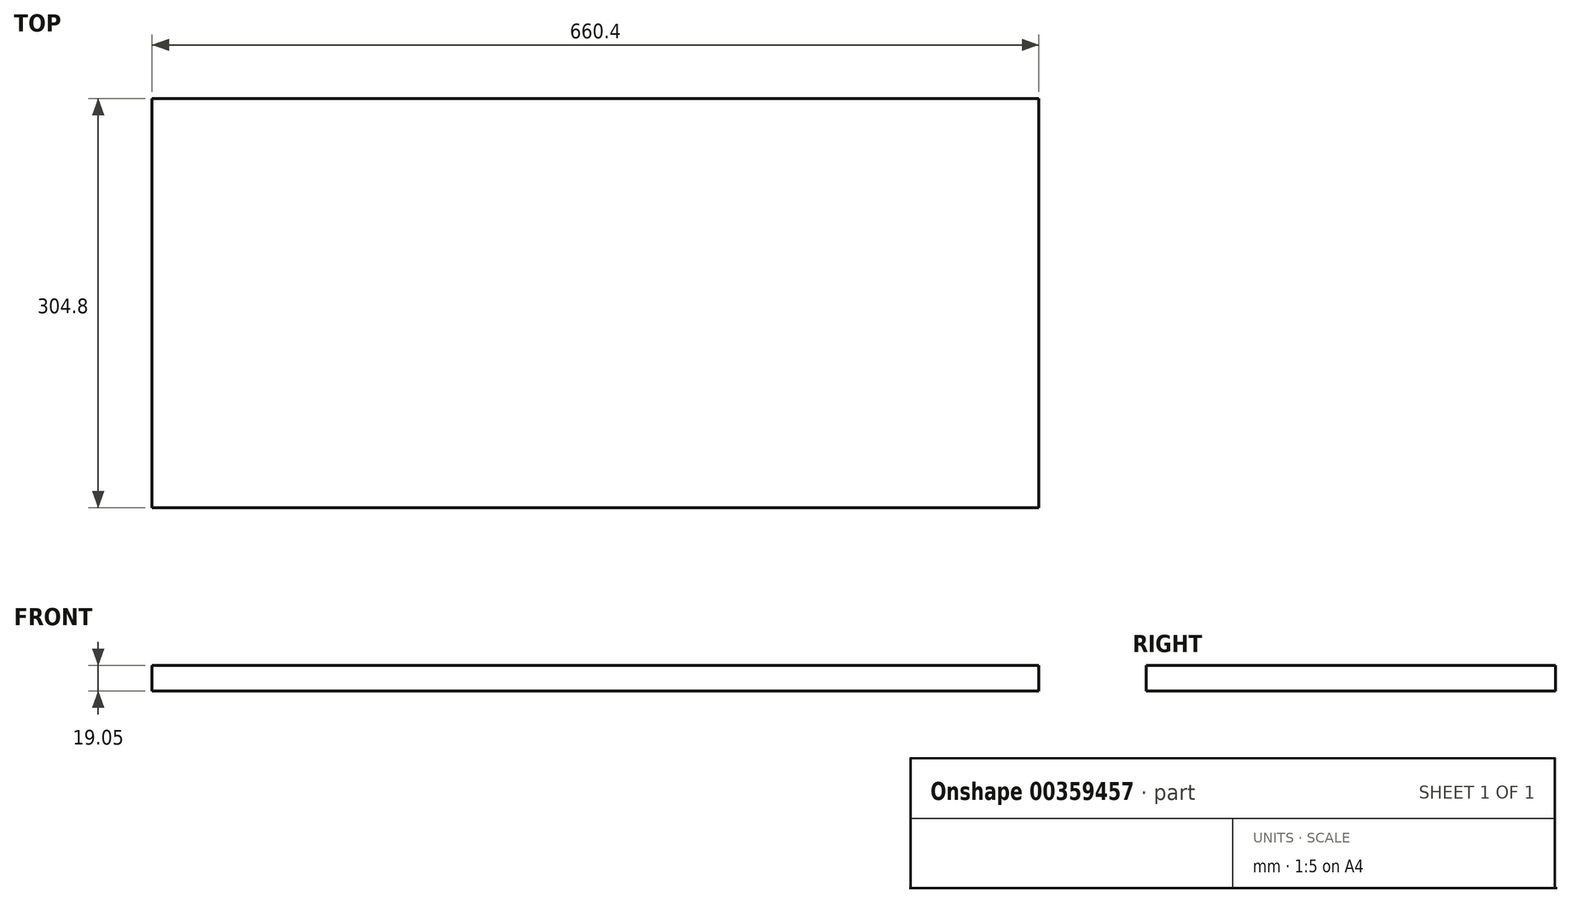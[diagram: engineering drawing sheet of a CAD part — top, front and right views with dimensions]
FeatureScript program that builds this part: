
annotation { "Feature Type Name" : "Feature", "Feature Type Description" : "" }
export const myFeature = defineFeature(function(context is Context, id is Id, definition is map)
    precondition{}
    {
        {
            var Q0;
            Q0=qCreatedBy(makeId("Top.planeOp"),FACE);
            var sketch = newSketch(context, id + "F0", { "sketchPlane" : qUnion([Q0])});
            skLineSegment(sketch, "E0.bottom", {"start": v(0, 0) * mm, "end": v(660.4, 0) * mm});
            skLineSegment(sketch, "E0.top", {"start": v(0, 304.8) * mm, "end": v(660.4, 304.8) * mm});
            skLineSegment(sketch, "E0.left", {"start": v(0, 0) * mm, "end": v(0, 304.8) * mm});
            skLineSegment(sketch, "E0.right", {"start": v(660.4, 0) * mm, "end": v(660.4, 304.8) * mm});
            skSolve(sketch);
        }
        {
            var Q0;
            Q0=makeQuery(id+"F0.imprint","IMPRINT",FACE,{"disambiguationData":[TD([[makeQuery(id+"F0.imprint","IMPRINT",EDGE,{"derivedFrom":sQuery(id+"F0.wireOp",EDGE,"E0.bottom")}),1.0]])]});
            extrude(context, id + "F1", {"entities" : qUnion([Q0]), "depth" : 19.05 * mm});
        }
    });
